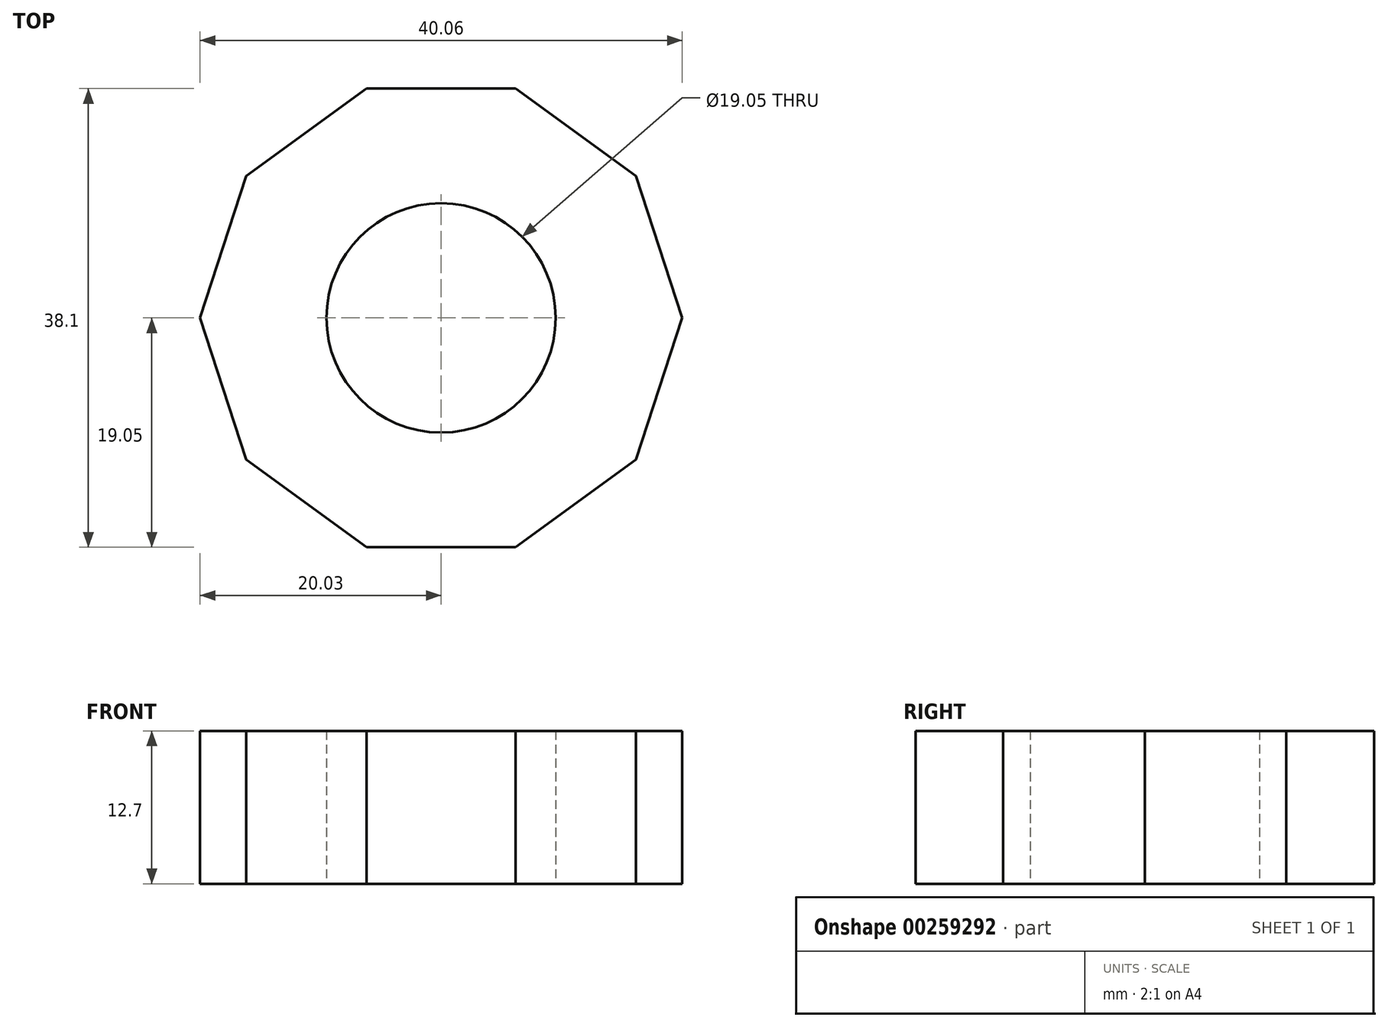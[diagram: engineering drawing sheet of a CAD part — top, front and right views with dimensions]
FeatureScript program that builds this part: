
annotation { "Feature Type Name" : "Feature", "Feature Type Description" : "" }
export const myFeature = defineFeature(function(context is Context, id is Id, definition is map)
    precondition{}
    {
        {
            var Q0;
            Q0=qCreatedBy(makeId("Top.planeOp"),FACE);
            var sketch = newSketch(context, id + "F0", { "sketchPlane" : qUnion([Q0])});
            skCircle(sketch, "E0.cCircle", {"center": v(0, 0) * mm, "radius": 19.05 * mm, "construction": true});
            skLineSegment(sketch, "E0.0", {"start": v(6.19, 19.05) * mm, "end": v(16.2, 11.77) * mm});
            skLineSegment(sketch, "E0.1", {"start": v(16.2, 11.77) * mm, "end": v(20.03, 0) * mm});
            skLineSegment(sketch, "E0.2", {"start": v(20.03, 0) * mm, "end": v(16.2, -11.77) * mm});
            skLineSegment(sketch, "E0.3", {"start": v(16.2, -11.77) * mm, "end": v(6.19, -19.05) * mm});
            skLineSegment(sketch, "E0.4", {"start": v(6.19, -19.05) * mm, "end": v(-6.19, -19.05) * mm});
            skLineSegment(sketch, "E0.5", {"start": v(-6.19, -19.05) * mm, "end": v(-16.2, -11.77) * mm});
            skLineSegment(sketch, "E0.6", {"start": v(-16.2, -11.77) * mm, "end": v(-20.03, 0) * mm});
            skLineSegment(sketch, "E0.7", {"start": v(-20.03, 0) * mm, "end": v(-16.2, 11.77) * mm});
            skLineSegment(sketch, "E0.8", {"start": v(-16.2, 11.77) * mm, "end": v(-6.19, 19.05) * mm});
            skLineSegment(sketch, "E0.9", {"start": v(-6.19, 19.05) * mm, "end": v(6.19, 19.05) * mm});
            skPoint(sketch, "E0.0.midPoint", {"position": v(11.2, 15.41) * mm});
            skCircle(sketch, "E1", {"center": v(0, 0) * mm, "radius": 9.53 * mm});
            skSolve(sketch);
        }
        {
            var Q0;
            Q0 = qSketchRegion(id + "F0", true);
            extrude(context, id + "F1", {"entities" : qUnion([Q0]), "depth" : 12.7 * mm});
        }
    });
